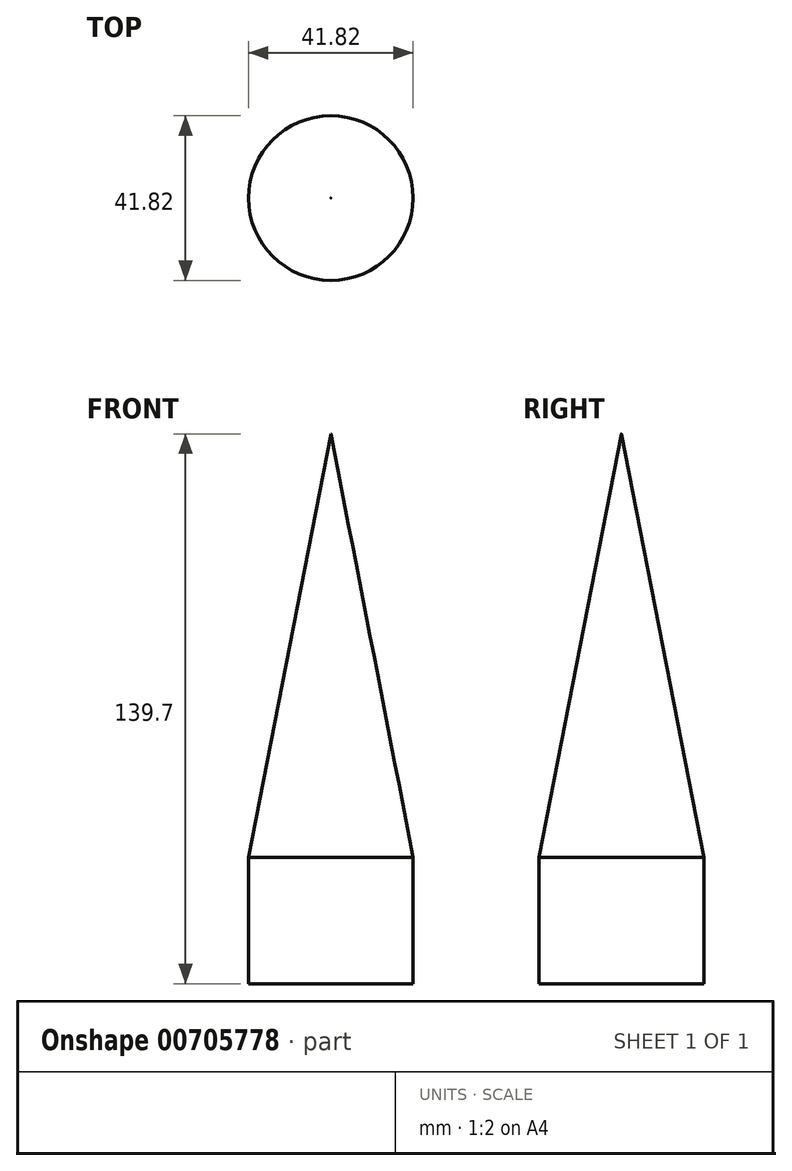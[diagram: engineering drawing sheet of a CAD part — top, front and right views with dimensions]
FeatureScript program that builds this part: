
annotation { "Feature Type Name" : "Feature", "Feature Type Description" : "" }
export const myFeature = defineFeature(function(context is Context, id is Id, definition is map)
    precondition{}
    {
        {
            var Q0;
            Q0=qCreatedBy(makeId("Top.planeOp"),FACE);
            var sketch = newSketch(context, id + "F0", { "sketchPlane" : qUnion([Q0])});
            skCircle(sketch, "E0", {"center": v(0, 0) * mm, "radius": 20.9 * mm});
            skSolve(sketch);
        }
        {
            var Q0;
            Q0=makeQuery(id+"F0.imprint","IMPRINT",FACE,{"disambiguationData":[TD([[makeQuery(id+"F0.imprint","IMPRINT",EDGE,{"derivedFrom":sQuery(id+"F0.wireOp",EDGE,"E0")}),1.0]])]});
            extrude(context, id + "F1", {"entities" : qUnion([Q0]), "depth" : 139.7 * mm, "offsetDistance" : 25.4 * mm});
        }
        {
            var Q0;
            Q0=makeQuery(id+"F1.opExtrude","CAP_EDGE",EDGE,{"disambiguationData":[OSD([sQuery(id+"F0.wireOp",EDGE,"E0")])],"isStart":false});
            chamfer(context, id + "F2", {"entities" : qUnion([Q0]), "chamferType" : ChamferType.OFFSET_ANGLE, "width" : 107.54 * mm, "oppositeDirection" : true, "angle" : 11 * degree});
        }
    });
